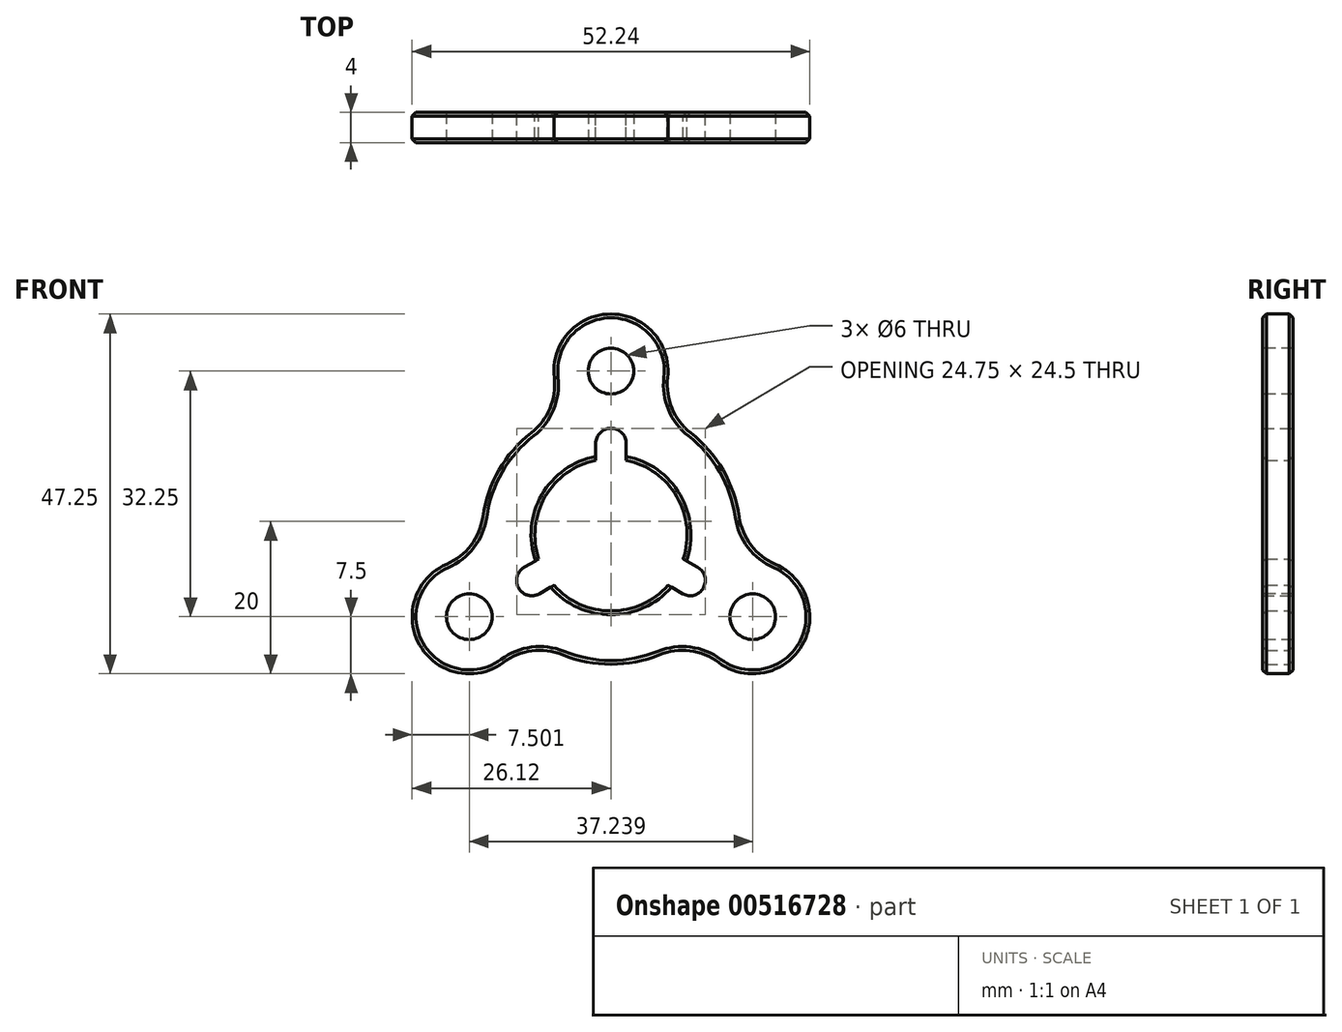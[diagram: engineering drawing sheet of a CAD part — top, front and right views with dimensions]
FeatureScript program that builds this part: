
annotation { "Feature Type Name" : "Feature", "Feature Type Description" : "" }
export const myFeature = defineFeature(function(context is Context, id is Id, definition is map)
    precondition{}
    {
        {
            var Q0;
            Q0=qCreatedBy(makeId("Front.planeOp"),FACE);
            var sketch = newSketch(context, id + "F0", { "sketchPlane" : qUnion([Q0])});
            skCircle(sketch, "E0", {"center": v(0, 0) * mm, "radius": 10 * mm});
            skArc(sketch, "E1", {"start": v(-25.11, 14.5) * mm, "mid": v(-29, 0) * mm, "end": v(-25.11, -14.5) * mm});
            skLineSegment(sketch, "E2", {"start": v(0, 0) * mm, "end": v(0, -29) * mm, "construction": true});
            skLineSegment(sketch, "E3", {"start": v(-25.11, 14.5) * mm, "end": v(0, 0) * mm, "construction": true});
            skLineSegment(sketch, "E4", {"start": v(25.11, 14.5) * mm, "end": v(0, 0) * mm, "construction": true});
            skLineSegment(sketch, "E5.MirrorCS", {"start": v(-25.11, -14.5) * mm, "end": v(0, 0) * mm, "construction": true});
            skLineSegment(sketch, "E6.MirrorCS", {"start": v(25.11, -14.5) * mm, "end": v(0, 0) * mm, "construction": true});
            skCircle(sketch, "E7", {"center": v(0, 0) * mm, "radius": 21.5 * mm, "construction": true});
            skArc(sketch, "E8", {"start": v(7.45, 20.63) * mm, "mid": v(0, 29) * mm, "end": v(-7.45, 20.63) * mm});
            skArc(sketch, "E9", {"start": v(14.14, -16.77) * mm, "mid": v(25.11, -14.5) * mm, "end": v(21.59, -3.86) * mm});
            skArc(sketch, "E10", {"start": v(-21.59, -3.86) * mm, "mid": v(-25.11, -14.5) * mm, "end": v(-14.14, -16.77) * mm});
            skArc(sketch, "E11", {"start": v(-10.47, 13.4) * mm, "mid": v(-14.72, 8.5) * mm, "end": v(-16.83, 2.37) * mm});
            skArc(sketch, "E12.trimOffspring", {"start": v(0, -29) * mm, "mid": v(14.5, -25.11) * mm, "end": v(25.11, -14.5) * mm});
            skArc(sketch, "E13.trimOffspring", {"start": v(-6.37, -15.76) * mm, "mid": v(0, -17) * mm, "end": v(6.37, -15.76) * mm});
            skArc(sketch, "E14.trimOffspring", {"start": v(16.83, 2.37) * mm, "mid": v(14.72, 8.5) * mm, "end": v(10.47, 13.4) * mm});
            skArc(sketch, "E15.trimOffspring", {"start": v(25.11, 14.5) * mm, "mid": v(14.5, 25.11) * mm, "end": v(0, 29) * mm});
            skPoint(sketch, "E16.visualSharp", {"position": v(-5.27, 16.16) * mm});
            skArc(sketch, "E16.filletArc", {"start": v(-10.47, 13.4) * mm, "mid": v(-8.01, 16.62) * mm, "end": v(-7.45, 20.63) * mm});
            skPoint(sketch, "E17.visualSharp", {"position": v(-16.63, -3.52) * mm});
            skArc(sketch, "E17.filletArc", {"start": v(-21.59, -3.86) * mm, "mid": v(-18.4, -1.37) * mm, "end": v(-16.83, 2.37) * mm});
            skPoint(sketch, "E18.visualSharp", {"position": v(-11.36, -12.64) * mm});
            skArc(sketch, "E18.filletArc", {"start": v(-6.37, -15.76) * mm, "mid": v(-10.38, -15.25) * mm, "end": v(-14.14, -16.77) * mm});
            skPoint(sketch, "E19.visualSharp", {"position": v(11.36, -12.64) * mm});
            skArc(sketch, "E19.filletArc", {"start": v(14.14, -16.77) * mm, "mid": v(10.38, -15.25) * mm, "end": v(6.37, -15.76) * mm});
            skPoint(sketch, "E20.visualSharp", {"position": v(16.63, -3.52) * mm});
            skArc(sketch, "E20.filletArc", {"start": v(16.83, 2.37) * mm, "mid": v(18.4, -1.37) * mm, "end": v(21.59, -3.86) * mm});
            skPoint(sketch, "E21.visualSharp", {"position": v(5.27, 16.16) * mm});
            skArc(sketch, "E21.filletArc", {"start": v(7.45, 20.63) * mm, "mid": v(8.01, 16.62) * mm, "end": v(10.47, 13.4) * mm});
            skSolve(sketch);
        }
        {
            var Q0;
            Q0=qSketchRegion(id+"F0",true);
            extrude(context, id + "F1", {"entities" : qUnion([Q0]), "depth" : 2 * mm, "offsetDistance" : 25 * mm, "hasSecondDirection" : true, "secondDirectionOppositeDirection" : true, "secondDirectionDepth" : 2 * mm});
        }
        {
            var Q0;
            Q0=makeQuery(id+"F1.opExtrude","CAP_FACE",FACE,{"disambiguationData":[OSD([sQuery(id+"F0.wireOp",EDGE,"E0"),sQuery(id+"F0.wireOp",EDGE,"E1")])],"isStart":false});
            var sketch = newSketch(context, id + "F2", { "sketchPlane" : qUnion([Q0])});
            skLineSegment(sketch, "E22", {"start": v(0, 0) * mm, "end": v(0, 29) * mm, "construction": true});
            skLineSegment(sketch, "E23", {"start": v(0, 0) * mm, "end": v(-25.11, -14.5) * mm, "construction": true});
            skLineSegment(sketch, "E24", {"start": v(0, 0) * mm, "end": v(25.11, -14.5) * mm, "construction": true});
            skPoint(sketch, "E25", {"position": v(0, 21.5) * mm});
            skPoint(sketch, "E26", {"position": v(-18.62, -10.75) * mm});
            skPoint(sketch, "E27", {"position": v(18.62, -10.75) * mm});
            skCircle(sketch, "E28", {"center": v(0, 0) * mm, "radius": 21.5 * mm, "construction": true});
            skSolve(sketch);
        }
        {
            var Q0;
            Q0=sQuery(id+"F2.wireOp",VERTEX,"E25");
            var Q1;
            Q1=sQuery(id+"F2.wireOp",VERTEX,"E26");
            var Q2;
            Q2=sQuery(id+"F2.wireOp",VERTEX,"E27");
            var Q3;
            Q3=makeQuery(id+"F1.opExtrude","SWEPT_BODY",BODY,{"disambiguationData":[OSD([sQuery(id+"F0.wireOp",EDGE,"E0"),sQuery(id+"F0.wireOp",EDGE,"E1")])]});
            hole(context, id + "F3", {"style" : HoleStyle.SIMPLE, "endStyle" : HoleEndStyle.THROUGH, "holeDiameter" : 6 * mm, "isTappedThrough" : true, "tappedDepth" : 12 * mm, "tapClearance" : 3, "locations" : qUnion([Q0, Q1, Q2]), "scope" : qUnion([Q3])});
        }
        {
            var Q0;
            Q0=makeQuery(id+"F1.opExtrude","CAP_EDGE",EDGE,{"disambiguationData":[OSD([sQuery(id+"F0.wireOp",EDGE,"E1")])],"isStart":false});
            var Q1;
            Q1=makeQuery(id+"F1.opExtrude","CAP_EDGE",EDGE,{"disambiguationData":[OSD([sQuery(id+"F0.wireOp",EDGE,"E0")])],"isStart":false});
            var Q2;
            Q2=makeQuery(id+"F1.opExtrude","SWEPT_FACE",FACE,{"disambiguationData":[OSD([sQuery(id+"F0.wireOp",EDGE,"E0")])]});
            var Q3;
            Q3=makeQuery(id+"F1.opExtrude","SWEPT_FACE",FACE,{"disambiguationData":[OSD([sQuery(id+"F0.wireOp",EDGE,"E1")])]});
            chamfer(context, id + "F4", {"entities" : qUnion([Q0, Q1, Q2, Q3]), "width" : .5 * mm, "tangentPropagation" : true});
        }
        {
            var Q0;
            Q0=makeQuery(id+"F1.opExtrude","CAP_EDGE",EDGE,{"disambiguationData":[OSD([sQuery(id+"F0.wireOp",EDGE,"E8")])],"isStart":true});
            var Q1;
            Q1=makeQuery(id+"F1.opExtrude","CAP_EDGE",EDGE,{"disambiguationData":[OSD([sQuery(id+"F0.wireOp",EDGE,"E21.filletArc")])],"isStart":true});
            var Q2;
            Q2=makeQuery(id+"F1.opExtrude","CAP_EDGE",EDGE,{"disambiguationData":[OSD([sQuery(id+"F0.wireOp",EDGE,"E8")])],"isStart":false});
            chamfer(context, id + "F5", {"entities" : qUnion([Q0, Q1, Q2]), "width" : .5 * mm, "tangentPropagation" : true});
        }
        {
            var Q0;
            Q0=makeQuery(id+"F1.opExtrude","CAP_FACE",FACE,{"disambiguationData":[OSD([sQuery(id+"F0.wireOp",EDGE,"E0"),sQuery(id+"F0.wireOp",EDGE,"E8"),sQuery(id+"F0.wireOp",EDGE,"E9"),sQuery(id+"F0.wireOp",EDGE,"E10"),sQuery(id+"F0.wireOp",EDGE,"E11"),sQuery(id+"F0.wireOp",EDGE,"E13.trimOffspring"),sQuery(id+"F0.wireOp",EDGE,"E14.trimOffspring"),sQuery(id+"F0.wireOp",EDGE,"E16.filletArc"),sQuery(id+"F0.wireOp",EDGE,"E17.filletArc"),sQuery(id+"F0.wireOp",EDGE,"E18.filletArc"),sQuery(id+"F0.wireOp",EDGE,"E19.filletArc"),sQuery(id+"F0.wireOp",EDGE,"E20.filletArc"),sQuery(id+"F0.wireOp",EDGE,"E21.filletArc")])],"isStart":true});
            var sketch = newSketch(context, id + "F6", { "sketchPlane" : qUnion([Q0])});
            skArc(sketch, "E29.0", {"start": v(2, 9.8) * mm, "mid": v(0, 10) * mm, "end": v(-2, 9.8) * mm});
            skLineSegment(sketch, "E30", {"start": v(-2, 9.8) * mm, "end": v(-2, 12) * mm});
            skLineSegment(sketch, "E31", {"start": v(2, 9.8) * mm, "end": v(2, 12) * mm});
            skArc(sketch, "E32", {"start": v(2, 12) * mm, "mid": v(0, 14) * mm, "end": v(-2, 12) * mm});
            skLineSegment(sketch, "E33.1.0", {"start": v(-7.49, -6.63) * mm, "end": v(-9.4, -7.73) * mm});
            skArc(sketch, "E33.1.1", {"start": v(-9.49, -3.17) * mm, "mid": v(-8.66, -5) * mm, "end": v(-7.49, -6.63) * mm});
            skArc(sketch, "E33.1.2", {"start": v(-11.4, -4.27) * mm, "mid": v(-12.12, -7) * mm, "end": v(-9.4, -7.73) * mm});
            skLineSegment(sketch, "E33.1.3", {"start": v(-9.49, -3.17) * mm, "end": v(-11.4, -4.27) * mm});
            skLineSegment(sketch, "E33.2.0", {"start": v(9.49, -3.17) * mm, "end": v(11.4, -4.27) * mm});
            skArc(sketch, "E33.2.1", {"start": v(7.49, -6.63) * mm, "mid": v(8.66, -5) * mm, "end": v(9.49, -3.17) * mm});
            skArc(sketch, "E33.2.2", {"start": v(9.4, -7.73) * mm, "mid": v(12.12, -7) * mm, "end": v(11.4, -4.27) * mm});
            skLineSegment(sketch, "E33.2.3", {"start": v(7.49, -6.63) * mm, "end": v(9.4, -7.73) * mm});
            skSolve(sketch);
        }
        {
            var Q0;
            Q0 = qSketchRegion(id + "F6", true);
            extrude(context, id + "F7", {"entities" : qUnion([Q0]), "operationType" : NewBodyOperationType.REMOVE, "endBound" : BoundingType.THROUGH_ALL, "oppositeDirection" : true, "depth" : 25 * mm, "offsetDistance" : 25 * mm});
        }
    });
